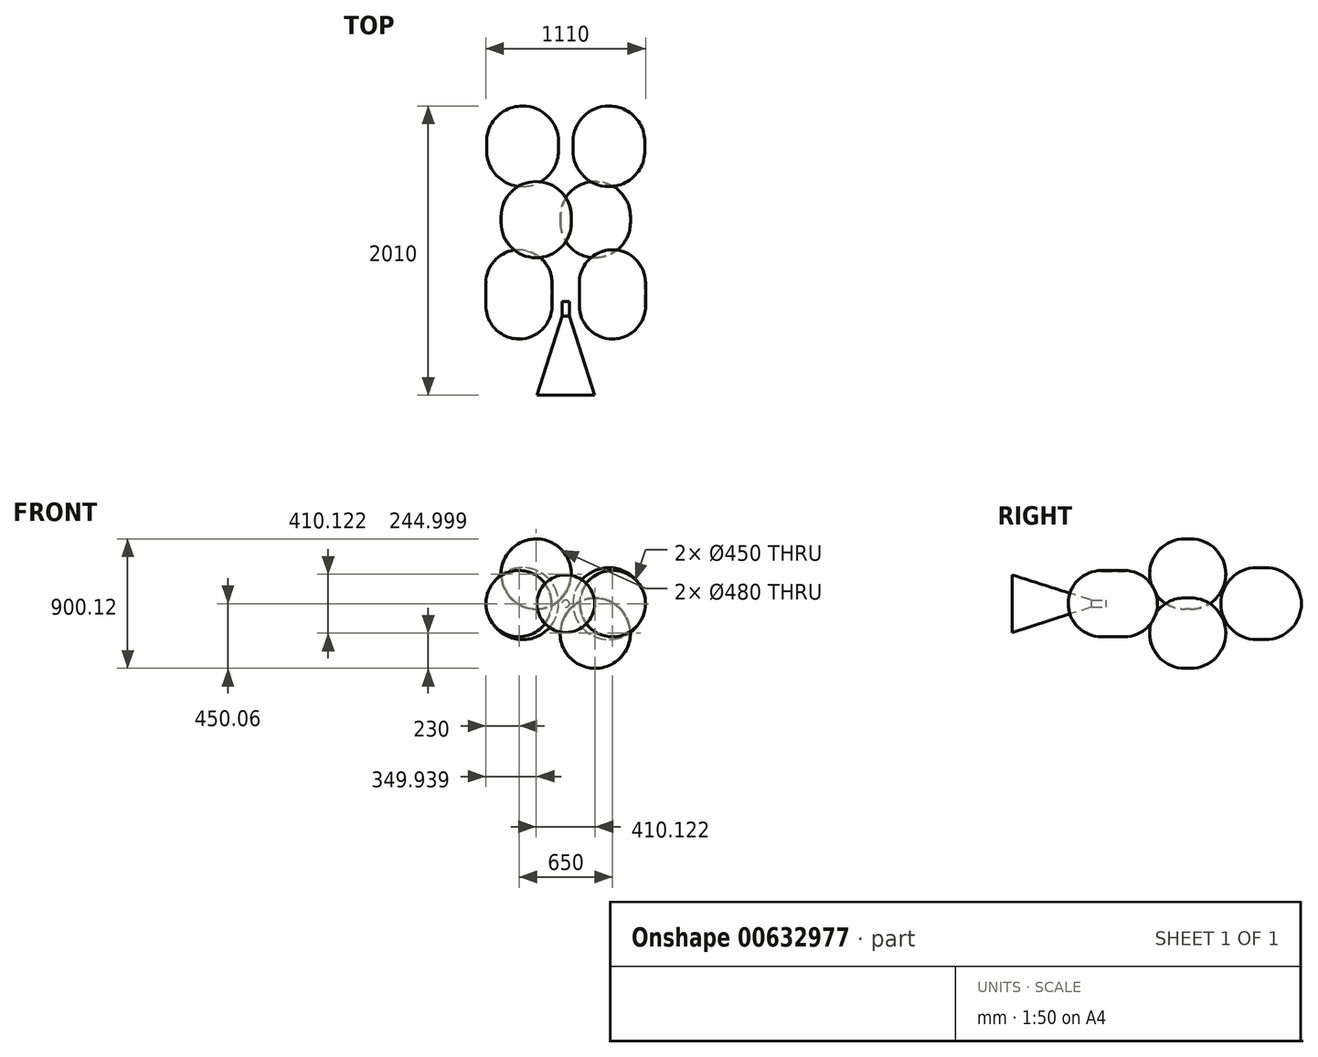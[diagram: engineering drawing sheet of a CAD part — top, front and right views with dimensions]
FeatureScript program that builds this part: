
annotation { "Feature Type Name" : "Feature", "Feature Type Description" : "" }
export const myFeature = defineFeature(function(context is Context, id is Id, definition is map)
    precondition{}
    {
        {
            var Q0;
            Q0=qCreatedBy(makeId("Front.planeOp"),FACE);
            var sketch = newSketch(context, id + "F0", { "sketchPlane" : qUnion([Q0])});
            skCircle(sketch, "E0", {"center": v(0, 0) * mm, "radius": 597 * mm});
            skCircle(sketch, "E1", {"center": v(0, 330) * mm, "radius": 220 * mm});
            skLineSegment(sketch, "E2", {"start": v(0, 330) * mm, "end": v(0, 0) * mm});
            skLineSegment(sketch, "E3", {"start": v(0, 0) * mm, "end": v(0, -330) * mm});
            skCircle(sketch, "E4", {"center": v(0, -330) * mm, "radius": 220 * mm});
            skLineSegment(sketch, "E5", {"start": v(0, 0) * mm, "end": v(-325, 0) * mm});
            skCircle(sketch, "E6", {"center": v(-325, 0) * mm, "radius": 225 * mm});
            skCircle(sketch, "E7", {"center": v(0, 0) * mm, "radius": 550 * mm});
            skLineSegment(sketch, "E8", {"start": v(0, 0) * mm, "end": v(325, 0) * mm});
            skCircle(sketch, "E9", {"center": v(325, 0) * mm, "radius": 225 * mm});
            skCircle(sketch, "E10", {"center": v(321.6, -326.6) * mm, "radius": 91.63 * mm});
            skSolve(sketch);
        }
        {
            var Q0;
            Q0=qCreatedBy(makeId("Top.planeOp"),FACE);
            var sketch = newSketch(context, id + "F1", { "sketchPlane" : qUnion([Q0])});
            skArc(sketch, "E11", {"start": v(-100, 80) * mm, "mid": v(-325, 305) * mm, "end": v(-550, 80) * mm});
            skArc(sketch, "E12", {"start": v(-550, -80) * mm, "mid": v(-325, -305) * mm, "end": v(-100, -80) * mm});
            skLineSegment(sketch, "E13", {"start": v(-325, -80) * mm, "end": v(-325, 80) * mm});
            skLineSegment(sketch, "E14", {"start": v(-550, 80) * mm, "end": v(-550, -80) * mm});
            skLineSegment(sketch, "E15", {"start": v(-100, 80) * mm, "end": v(-100, -80) * mm});
            skSolve(sketch);
        }
        {
            var Q0;
            Q0=qCreatedBy(makeId("Top.planeOp"),FACE);
            var sketch = newSketch(context, id + "F2", { "sketchPlane" : qUnion([Q0])});
            skLineSegment(sketch, "E16", {"start": v(-325, 310) * mm, "end": v(-325, -310) * mm});
            skArc(sketch, "E17", {"start": v(-325, -310) * mm, "mid": v(-162.37, -242.63) * mm, "end": v(-95, -80) * mm});
            skLineSegment(sketch, "E18", {"start": v(-95, 80) * mm, "end": v(-95, -80) * mm});
            skArc(sketch, "E19.trimOffspring", {"start": v(-95, 80) * mm, "mid": v(-162.37, 242.63) * mm, "end": v(-325, 310) * mm});
            skArc(sketch, "E20", {"start": v(-100, 80) * mm, "mid": v(-165.9, 239.1) * mm, "end": v(-325, 305) * mm});
            skArc(sketch, "E21", {"start": v(-325, -305) * mm, "mid": v(-165.9, -239.1) * mm, "end": v(-100, -80) * mm});
            skLineSegment(sketch, "E22", {"start": v(-100, 80) * mm, "end": v(-100, -80) * mm});
            skSolve(sketch);
        }
        {
            var Q0;
            {var subQ0=sQuery(id+"F2.wireOp",EDGE,"E17");Q0=makeQuery(id+"F2.imprint","IMPRINT",FACE,{"disambiguationData":[TD([[makeQuery(id+"F2.imprint","IMPRINT",EDGE,{"derivedFrom":subQ0}),1.0]])]});}
            var Q1;
            Q1=sQuery(id+"F2.wireOp",EDGE,"E16");
            revolve(context, id + "F3", {"entities" : qUnion([Q0]), "axis" : qUnion([Q1]), "revolveType" : RevolveType.FULL});
        }
        {
            var Q0;
            Q0=qCreatedBy(makeId("Front.planeOp"),FACE);
            cPlane(context, id + "F4", {"entities" : qUnion([Q0]), "cplaneType" : CPlaneType.OFFSET, "offset" : 305 * mm, "oppositeDirection" : true, "width" : 150 * mm, "height" : 150 * mm});
        }
        {
            var Q0;
            Q0=qCreatedBy(makeId("Right.planeOp"),FACE);
            var sketch = newSketch(context, id + "F5", { "sketchPlane" : qUnion([Q0])});
            skLineSegment(sketch, "E23", {"start": v(0, 0) * mm, "end": v(461.7, 0) * mm});
            skSolve(sketch);
        }
        {
            var Q0;
            Q0=qCreatedBy(makeId("Right.planeOp"),FACE);
            var Q1;
            Q1=sQuery(id+"F5.wireOp",EDGE,"E23");
            cPlane(context, id + "F6", {"entities" : qUnion([Q0, Q1]), "cplaneType" : CPlaneType.LINE_ANGLE, "offset" : 25 * mm, "angle" : 45 * degree, "oppositeDirection" : true, "width" : 150 * mm, "height" : 150 * mm});
        }
        {
            var Q0;
            Q0=qCreatedBy(id+"F6.planeOp",FACE);
            var sketch = newSketch(context, id + "F7", { "sketchPlane" : qUnion([Q0])});
            skArc(sketch, "E24", {"start": v(-500, 50) * mm, "mid": v(-260, 290) * mm, "end": v(-500, 530) * mm});
            skLineSegment(sketch, "E25", {"start": v(-500, 290) * mm, "end": v(-540, 290) * mm});
            skArc(sketch, "E26", {"start": v(-540, 530) * mm, "mid": v(-780, 290) * mm, "end": v(-540, 50) * mm});
            skArc(sketch, "E27", {"start": v(-540, 535) * mm, "mid": v(-785, 290) * mm, "end": v(-540, 45) * mm});
            skLineSegment(sketch, "E28", {"start": v(-540, 535) * mm, "end": v(-500, 535) * mm});
            skLineSegment(sketch, "E29", {"start": v(-540, 45) * mm, "end": v(-500, 45) * mm});
            skArc(sketch, "E30.trimOffspring", {"start": v(-500, 45) * mm, "mid": v(-255, 290) * mm, "end": v(-500, 535) * mm});
            skLineSegment(sketch, "E31", {"start": v(-540, 50) * mm, "end": v(-500, 50) * mm});
            skLineSegment(sketch, "E32", {"start": v(-540, 530) * mm, "end": v(-500, 530) * mm});
            skLineSegment(sketch, "E33", {"start": v(-540, 290) * mm, "end": v(-785, 290) * mm});
            skLineSegment(sketch, "E34", {"start": v(-500, 290) * mm, "end": v(-255, 290) * mm});
            skSolve(sketch);
        }
        {
            var Q0;
            {var subQ0=sQuery(id+"F7.wireOp",EDGE,"E28");Q0=makeQuery(id+"F7.imprint","IMPRINT",FACE,{"disambiguationData":[TD([[makeQuery(id+"F7.imprint","IMPRINT",EDGE,{"derivedFrom":subQ0}),-1.0]])]});}
            var Q1;
            Q1=sQuery(id+"F7.wireOp",EDGE,"E33");
            revolve(context, id + "F8", {"entities" : qUnion([Q0]), "axis" : qUnion([Q1]), "revolveType" : RevolveType.FULL});
        }
        {
            var Q0;
            Q0=qCreatedBy(makeId("Front.planeOp"),FACE);
            cPlane(context, id + "F9", {"entities" : qUnion([Q0]), "cplaneType" : CPlaneType.OFFSET, "offset" : 785 * mm, "oppositeDirection" : true, "width" : 150 * mm, "height" : 150 * mm});
        }
        {
            var Q0;
            Q0=qCreatedBy(makeId("Top.planeOp"),FACE);
            var sketch = newSketch(context, id + "F10", { "sketchPlane" : qUnion([Q0])});
            skLineSegment(sketch, "E35", {"start": v(-300, 750) * mm, "end": v(-300, 1000) * mm});
            skArc(sketch, "E36", {"start": v(-550, 1000) * mm, "mid": v(-300, 750) * mm, "end": v(-50, 1000) * mm});
            skLineSegment(sketch, "E37", {"start": v(-300, 1000) * mm, "end": v(-300, 1060) * mm});
            skLineSegment(sketch, "E38", {"start": v(-550, 1060) * mm, "end": v(-550, 1000) * mm});
            skLineSegment(sketch, "E39", {"start": v(-50, 1060) * mm, "end": v(-50, 1000) * mm});
            skArc(sketch, "E40.trimOffspring", {"start": v(-50, 1060) * mm, "mid": v(-300, 1310) * mm, "end": v(-550, 1060) * mm});
            skLineSegment(sketch, "E41", {"start": v(-300, 1060) * mm, "end": v(-300, 1310) * mm});
            skSolve(sketch);
        }
        {
            var Q0;
            {var subQ2=sQuery(id+"F10.wireOp",EDGE,"E35");Q0=makeQuery(id+"F10.imprint","IMPRINT",FACE,{"disambiguationData":[TD([[makeQuery(id+"F10.imprint","IMPRINT",EDGE,{"derivedFrom":subQ2}),1.0]])]});}
            var Q1;
            Q1=sQuery(id+"F10.wireOp",EDGE,"E41");
            revolve(context, id + "F11", {"entities" : qUnion([Q0]), "axis" : qUnion([Q1]), "revolveType" : RevolveType.FULL});
        }
        {
            var Q0;
            Q0=qCreatedBy(makeId("Right.planeOp"),FACE);
            var sketch = newSketch(context, id + "F12", { "sketchPlane" : qUnion([Q0])});
            skLineSegment(sketch, "E42", {"start": v(0, 0) * mm, "end": v(-700, 0) * mm});
            skLineSegment(sketch, "E43", {"start": v(-700, 200) * mm, "end": v(-700, 0) * mm});
            skLineSegment(sketch, "E44", {"start": v(-700, 200) * mm, "end": v(-150, 25) * mm});
            skLineSegment(sketch, "E45", {"start": v(-50, 25) * mm, "end": v(-150, 25) * mm});
            skLineSegment(sketch, "E46", {"start": v(-50, 25) * mm, "end": v(-50, 0) * mm});
            skSolve(sketch);
        }
        {
            var Q0;
            {var subQ0=sQuery(id+"F12.wireOp",EDGE,"E43");Q0=makeQuery(id+"F12.imprint","IMPRINT",FACE,{"disambiguationData":[TD([[makeQuery(id+"F12.imprint","IMPRINT",EDGE,{"derivedFrom":subQ0}),1.0]])]});}
            var Q1;
            Q1=sQuery(id+"F12.wireOp",EDGE,"E42");
            revolve(context, id + "F13", {"entities" : qUnion([Q0]), "axis" : qUnion([Q1]), "revolveType" : RevolveType.FULL});
        }
        {
            var Q0;
            Q0=makeQuery(id+"F3.opRevolve","SWEPT_BODY",BODY,{"disambiguationData":[OSD([sQuery(id+"F2.wireOp",EDGE,"E16"),sQuery(id+"F2.wireOp",EDGE,"E17"),sQuery(id+"F2.wireOp",EDGE,"E18"),sQuery(id+"F2.wireOp",EDGE,"E19.trimOffspring"),sQuery(id+"F2.wireOp",EDGE,"E20"),sQuery(id+"F2.wireOp",EDGE,"E21"),sQuery(id+"F2.wireOp",EDGE,"E22")])]});
            var Q1;
            Q1=sQuery(id+"F12.wireOp",EDGE,"E42");
            circularPattern(context, id + "F14", {"entities" : qUnion([Q0]), "axis" : qUnion([Q1]), "angle" : 360 * degree, "instanceCount" : 2, "oppositeDirection" : true, "equalSpace" : true});
        }
        {
            var Q0;
            Q0=makeQuery(id+"F8.opRevolve","SWEPT_BODY",BODY,{"disambiguationData":[OSD([sQuery(id+"F7.wireOp",EDGE,"E24"),sQuery(id+"F7.wireOp",EDGE,"E26"),sQuery(id+"F7.wireOp",EDGE,"E27"),sQuery(id+"F7.wireOp",EDGE,"E28"),sQuery(id+"F7.wireOp",EDGE,"E30.trimOffspring"),sQuery(id+"F7.wireOp",EDGE,"E32"),sQuery(id+"F7.wireOp",EDGE,"E33"),sQuery(id+"F7.wireOp",EDGE,"E34")])]});
            var Q1;
            Q1=sQuery(id+"F12.wireOp",EDGE,"E42");
            circularPattern(context, id + "F15", {"entities" : qUnion([Q0]), "axis" : qUnion([Q1]), "angle" : 360 * degree, "instanceCount" : 2, "oppositeDirection" : true, "equalSpace" : true});
        }
        {
            var Q0;
            Q0=makeQuery(id+"F11.opRevolve","SWEPT_BODY",BODY,{"disambiguationData":[OSD([sQuery(id+"F10.wireOp",EDGE,"E35"),sQuery(id+"F10.wireOp",EDGE,"E36"),sQuery(id+"F10.wireOp",EDGE,"E37"),sQuery(id+"F10.wireOp",EDGE,"E38"),sQuery(id+"F10.wireOp",EDGE,"E40.trimOffspring"),sQuery(id+"F10.wireOp",EDGE,"E41")])]});
            var Q1;
            Q1=sQuery(id+"F12.wireOp",EDGE,"E42");
            circularPattern(context, id + "F16", {"entities" : qUnion([Q0]), "axis" : qUnion([Q1]), "angle" : 360 * degree, "instanceCount" : 2, "oppositeDirection" : true, "equalSpace" : true});
        }
    });
